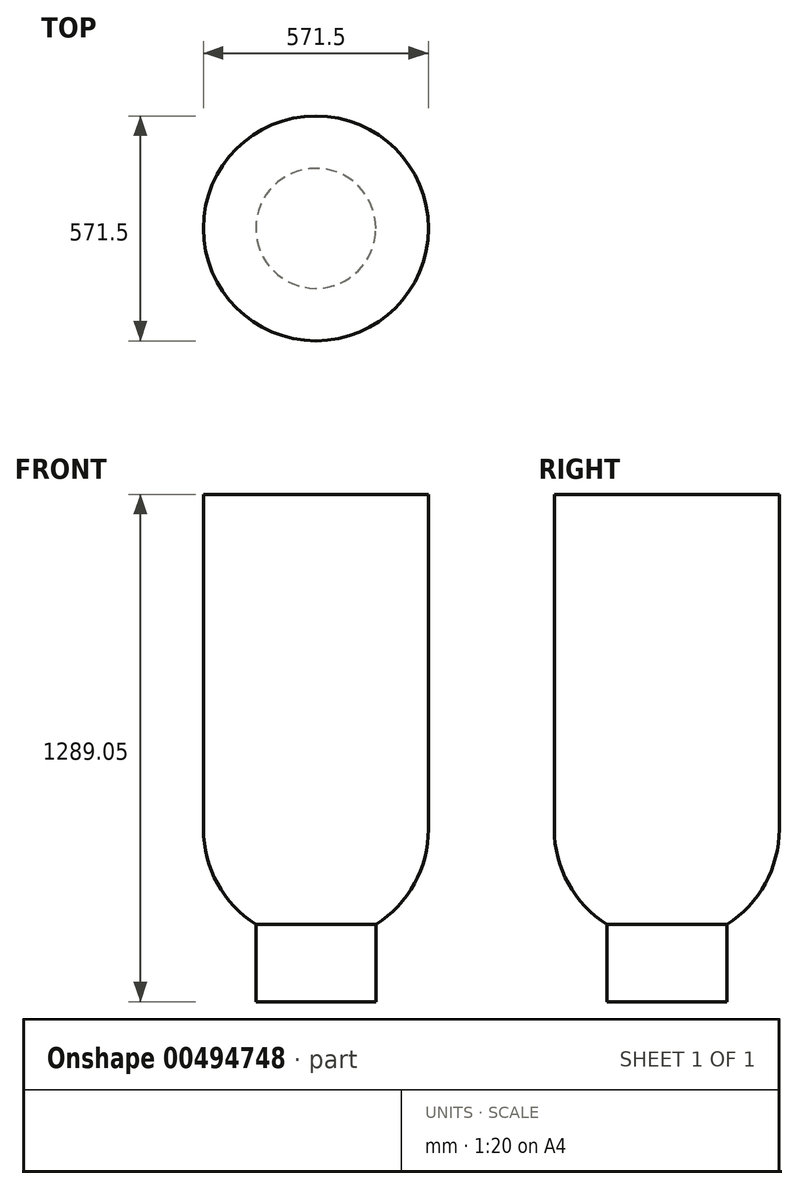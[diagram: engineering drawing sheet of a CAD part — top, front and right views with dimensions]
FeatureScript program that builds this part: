
annotation { "Feature Type Name" : "Feature", "Feature Type Description" : "" }
export const myFeature = defineFeature(function(context is Context, id is Id, definition is map)
    precondition{}
    {
        {
            var Q0;
            Q0=qCreatedBy(makeId("Top.planeOp"),FACE);
            var sketch = newSketch(context, id + "F0", { "sketchPlane" : qUnion([Q0])});
            skCircle(sketch, "E0", {"center": v(0, 0) * mm, "radius": 285.75 * mm});
            skLineSegment(sketch, "E1", {"start": v(0, 0) * mm, "end": v(285.75, 0) * mm});
            skLineSegment(sketch, "E2", {"start": v(0, 0) * mm, "end": v(-285.75, 0) * mm});
            skSolve(sketch);
        }
        {
            var Q0;
            {var subQ0=sQuery(id+"F0.wireOp",EDGE,"E1");Q0=makeQuery(id+"F0.imprint","IMPRINT",FACE,{"disambiguationData":[TD([[makeQuery(id+"F0.imprint","IMPRINT",EDGE,{"derivedFrom":subQ0}),1.0]])]});}
            var Q1;
            Q1=sQuery(id+"F0.wireOp",EDGE,"E1");
            revolve(context, id + "F1", {"entities" : qUnion([Q0]), "axis" : qUnion([Q1]), "revolveType" : RevolveType.ONE_DIRECTION, "oppositeDirection" : true, "angle" : 180 * degree});
        }
        {
            var Q0;
            Q0=makeQuery(id+"F1.opRevolve","CAP_FACE",FACE,{"disambiguationData":[OSD([sQuery(id+"F0.wireOp",EDGE,"E0"),sQuery(id+"F0.wireOp",EDGE,"E1"),sQuery(id+"F0.wireOp",EDGE,"E2")])],"isStart":true});
            var sketch = newSketch(context, id + "F2", { "sketchPlane" : qUnion([Q0])});
            skCircle(sketch, "E3", {"center": v(0, 0) * mm, "radius": 152.4 * mm});
            skSolve(sketch);
        }
        {
            var Q0;
            Q0 = qSketchRegion(id + "F2", true);
            extrude(context, id + "F3", {"entities" : qUnion([Q0]), "operationType" : NewBodyOperationType.ADD, "oppositeDirection" : true, "depth" : 438.15 * mm});
        }
        {
            var Q0;
            Q0=makeQuery(id+"F1.opRevolve","CAP_FACE",FACE,{"disambiguationData":[OSD([sQuery(id+"F0.wireOp",EDGE,"E0"),sQuery(id+"F0.wireOp",EDGE,"E1"),sQuery(id+"F0.wireOp",EDGE,"E2")])],"isStart":true});
            var sketch = newSketch(context, id + "F4", { "sketchPlane" : qUnion([Q0])});
            skCircle(sketch, "E4", {"center": v(0, 0) * mm, "radius": 285.75 * mm});
            skSolve(sketch);
        }
        {
            var Q0;
            Q0 = qSketchRegion(id + "F4", true);
            extrude(context, id + "F5", {"entities" : qUnion([Q0]), "operationType" : NewBodyOperationType.ADD, "depth" : 850.9 * mm});
        }
    });
